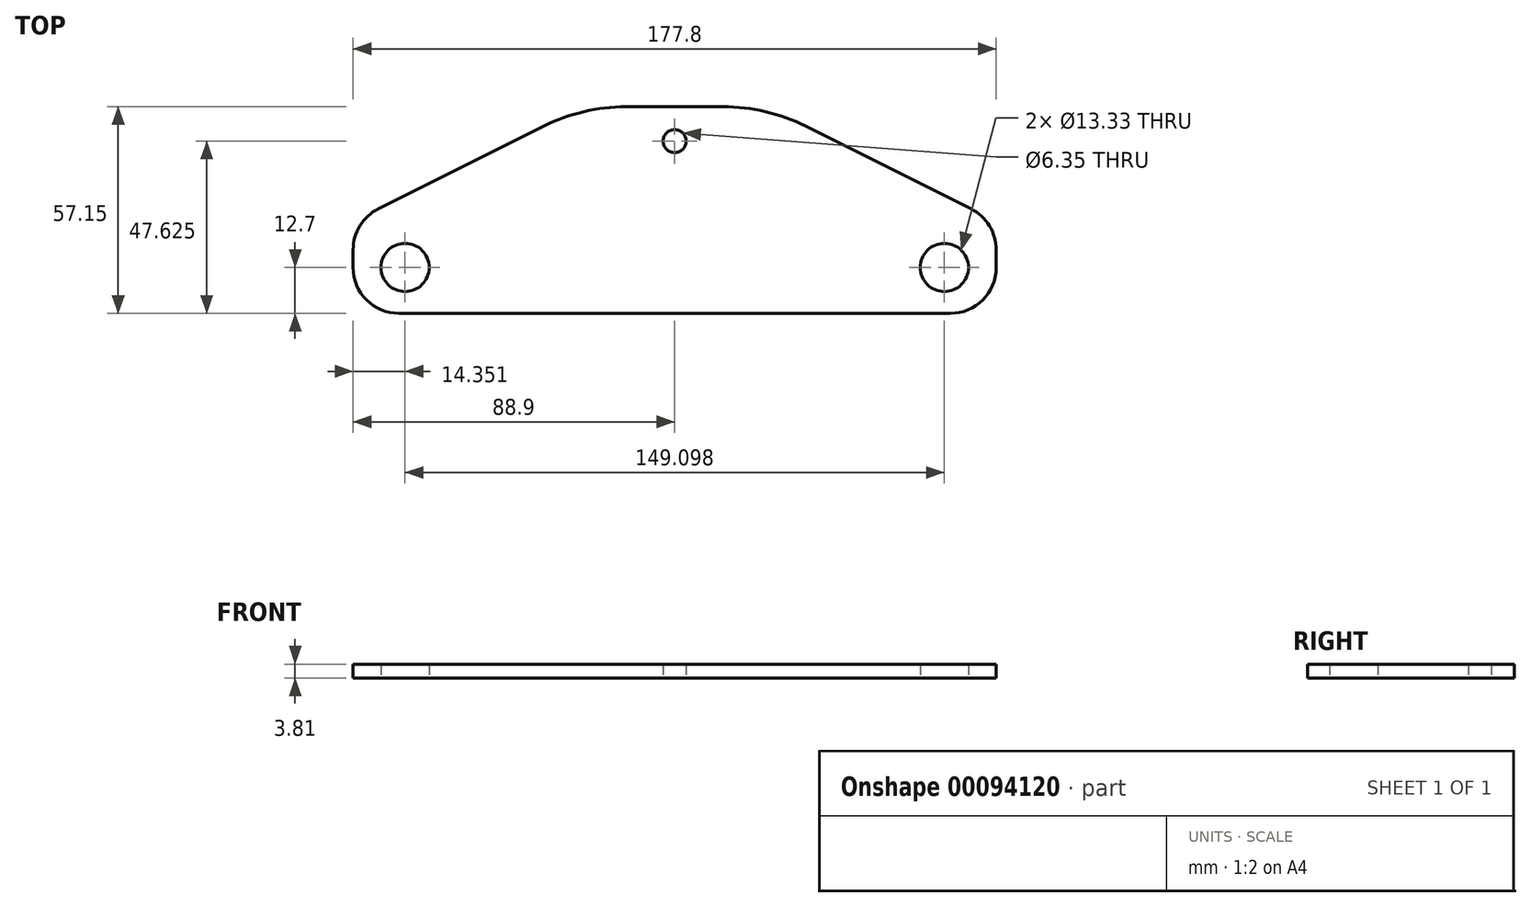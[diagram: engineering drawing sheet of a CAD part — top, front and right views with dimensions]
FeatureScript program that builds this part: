
annotation { "Feature Type Name" : "Feature", "Feature Type Description" : "" }
export const myFeature = defineFeature(function(context is Context, id is Id, definition is map)
    precondition{}
    {
        {
            var Q0;
            Q0=qCreatedBy(makeId("Top.planeOp"),FACE);
            var sketch = newSketch(context, id + "F0", { "sketchPlane" : qUnion([Q0])});
            skLineSegment(sketch, "E0.bottom", {"start": v(0, 0) * mm, "end": v(177.8, 0) * mm});
            skLineSegment(sketch, "E0.top", {"start": v(0, 25.4) * mm, "end": v(177.8, 25.4) * mm});
            skLineSegment(sketch, "E0.left", {"start": v(0, 0) * mm, "end": v(0, 25.4) * mm});
            skLineSegment(sketch, "E0.right", {"start": v(177.8, 0) * mm, "end": v(177.8, 25.4) * mm});
            skLineSegment(sketch, "E1", {"start": v(0, 25.4) * mm, "end": v(63.5, 57.15) * mm});
            skLineSegment(sketch, "E2", {"start": v(63.5, 57.15) * mm, "end": v(114.3, 57.15) * mm});
            skLineSegment(sketch, "E3", {"start": v(114.3, 57.15) * mm, "end": v(177.8, 25.4) * mm});
            skCircle(sketch, "E4", {"center": v(14.35, 12.7) * mm, "radius": 6.67 * mm});
            skCircle(sketch, "E5", {"center": v(163.45, 12.7) * mm, "radius": 6.67 * mm});
            skLineSegment(sketch, "E6", {"start": v(14.35, 12.7) * mm, "end": v(0, 12.7) * mm, "construction": true});
            skLineSegment(sketch, "E7", {"start": v(163.45, 12.7) * mm, "end": v(177.8, 12.7) * mm, "construction": true});
            skLineSegment(sketch, "E8", {"start": v(88.9, 57.15) * mm, "end": v(88.9, 25.4) * mm, "construction": true});
            skCircle(sketch, "E9", {"center": v(88.9, 47.62) * mm, "radius": 3.18 * mm});
            skSolve(sketch);
        }
        {
            var Q0;
            Q0=makeQuery(id+"F0.imprint","IMPRINT",FACE,{"disambiguationData":[TD([[makeQuery(id+"F0.imprint","IMPRINT",EDGE,{"derivedFrom":sQuery(id+"F0.wireOp",EDGE,"E0.bottom")}),1.0]])]});
            var Q1;
            Q1=makeQuery(id+"F0.imprint","IMPRINT",FACE,{"disambiguationData":[TD([[makeQuery(id+"F0.imprint","IMPRINT",EDGE,{"derivedFrom":sQuery(id+"F0.wireOp",EDGE,"E0.top")}),1.0]])]});
            extrude(context, id + "F1", {"entities" : qUnion([Q0, Q1]), "depth" : 3.8 * mm});
        }
        {
            var Q0;
            Q0=makeQuery(id+"F1.opExtrude","SWEPT_EDGE",EDGE,{"disambiguationData":[OSD([sQuery(id+"F0.wireOp",EDGE,"E1"),sQuery(id+"F0.wireOp",EDGE,"E2")])]});
            var Q1;
            Q1=makeQuery(id+"F1.opExtrude","SWEPT_EDGE",EDGE,{"disambiguationData":[OSD([sQuery(id+"F0.wireOp",EDGE,"E2"),sQuery(id+"F0.wireOp",EDGE,"E3")])]});
            fillet(context, id + "F2", {"entities" : qUnion([Q0, Q1]), "radius" : 50.8 * mm, "tangentPropagation" : true, "allowEdgeOverflow" : false});
        }
        {
            var Q0;
            Q0=makeQuery(id+"F1.opExtrude","SWEPT_EDGE",EDGE,{"disambiguationData":[OSD([sQuery(id+"F0.wireOp",EDGE,"E0.top"),sQuery(id+"F0.wireOp",EDGE,"E0.left"),sQuery(id+"F0.wireOp",EDGE,"E1")])]});
            var Q1;
            Q1=makeQuery(id+"F1.opExtrude","SWEPT_EDGE",EDGE,{"disambiguationData":[OSD([sQuery(id+"F0.wireOp",EDGE,"E0.bottom"),sQuery(id+"F0.wireOp",EDGE,"E0.left")])]});
            var Q2;
            Q2=makeQuery(id+"F1.opExtrude","SWEPT_EDGE",EDGE,{"disambiguationData":[OSD([sQuery(id+"F0.wireOp",EDGE,"E0.bottom"),sQuery(id+"F0.wireOp",EDGE,"E0.right")])]});
            var Q3;
            Q3=makeQuery(id+"F1.opExtrude","SWEPT_EDGE",EDGE,{"disambiguationData":[OSD([sQuery(id+"F0.wireOp",EDGE,"E0.top"),sQuery(id+"F0.wireOp",EDGE,"E0.right"),sQuery(id+"F0.wireOp",EDGE,"E3")])]});
            fillet(context, id + "F3", {"entities" : qUnion([Q0, Q1, Q2, Q3]), "radius" : 12.7 * mm, "tangentPropagation" : true, "allowEdgeOverflow" : false});
        }
    });
